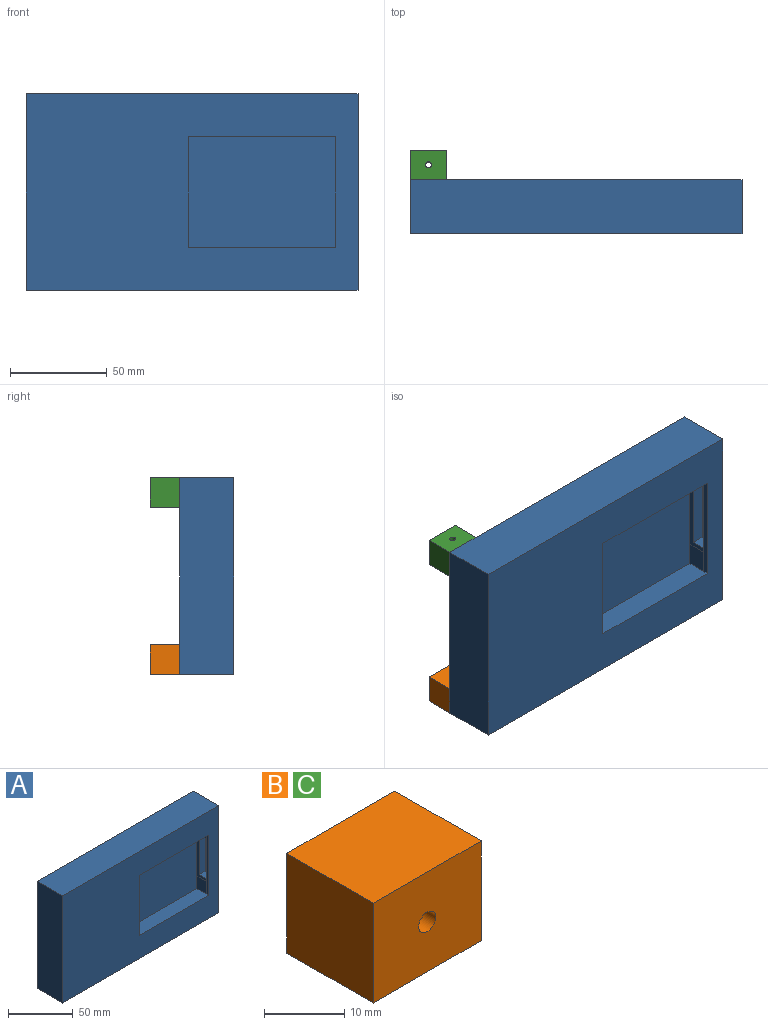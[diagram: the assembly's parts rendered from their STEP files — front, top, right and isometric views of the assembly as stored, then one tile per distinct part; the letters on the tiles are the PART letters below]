
ASSEMBLY  parts=3 mates=2
PART A: 29 faces, bbox 171.5x27.9x101.6 mm
  f0: plane 101.6x27.94mm, normal (-1,0,0), area 2838.7mm2, adj f1,f2,f3,f8
  f1: plane 171.45x27.94mm, normal (0,0,-1), area 4790.3mm2, adj f0,f3,f8,f14
  f2: plane 171.45x27.94mm, normal (0,0,1), area 4790.3mm2, adj f0,f3,f8,f14
  f3: plane 171.45x101.6mm, normal (0,1,0), area 17419.3mm2, adj f0,f1,f2,f14
  f4: plane 57.15x2.54mm, normal (-1,0,0), area 145.2mm2, adj f5,f7,f8,f13
  f5: plane 76.2x12.7mm, normal (0,0,1), area 967.7mm2, adj f4,f6,f8,f9,f19
  f6: plane 57.15x12.7mm, normal (1,0,0), area 725.8mm2, adj f5,f7,f8,f9
  f7: plane 76.2x12.7mm, normal (0,0,-1), area 967.7mm2, adj f4,f6,f8,f9,f19
  f8: plane 171.45x101.6mm, normal (0,-1,0), area 13064.5mm2, adj f0,f1,f2,f4,f5,f6,f7,f14
  f9: plane 76.2x57.15mm, normal (0,-1,0), area 4354.8mm2, adj f5,f6,f7,f19
  f10: plane 12.7x6.35mm, normal (0,0,-1), area 80.6mm2, adj f11,f13,f14,f28
  f11: plane 38.1x6.35mm, normal (0,-1,0), area 241.9mm2, adj f10,f12,f14,f28
  f12: plane 12.7x6.35mm, normal (0,0,1), area 80.6mm2, adj f11,f13,f14,f28
  f13: plane 168.91x96.52mm, normal (0,1,0), area 11235.5mm2, adj f4,f10,f12,f14,f15,f16,f17,f19
  f14: plane 101.6x27.94mm, normal (1,0,0), area 2354.8mm2, adj f1,f2,f3,f8,f10,f11,f12,f13
  f15: plane 96.52x22.86mm, normal (1,0,0), area 2206.4mm2, adj f13,f16,f17,f18
  f16: plane 166.37x22.86mm, normal (0,0,1), area 3803.2mm2, adj f13,f15,f18,f27
  f17: plane 166.37x22.86mm, normal (0,0,-1), area 3803.2mm2, adj f13,f15,f18,f27
  f18: plane 166.37x96.52mm, normal (0,-1,0), area 16058mm2, adj f15,f16,f17,f27
  f19: plane 62.23x12.7mm, normal (1,0,0), area 209.7mm2, adj f5,f7,f9,f13,f20,f22,f23
  f20: plane 78.74x12.7mm, normal (0,0,-1), area 1000mm2, adj f13,f19,f21,f23
  f21: plane 62.23x12.7mm, normal (-1,0,0), area 790.3mm2, adj f13,f20,f22,f23
  f22: plane 78.74x12.7mm, normal (0,0,1), area 1000mm2, adj f13,f19,f21,f23
  f23: plane 78.74x62.23mm, normal (0,1,0), area 4900mm2, adj f19,f20,f21,f22
  f24: plane 15.24x3.81mm, normal (0,0,1), area 58.1mm2, adj f13,f25,f27,f28
  f25: plane 43.18x3.81mm, normal (0,1,0), area 164.5mm2, adj f24,f26,f27,f28
  f26: plane 15.24x3.81mm, normal (0,0,-1), area 58.1mm2, adj f13,f25,f27,f28
  f27: plane 96.52x22.86mm, normal (-1,0,0), area 1548.4mm2, adj f13,f16,f17,f18,f24,f25,f26
  f28: plane 43.18x15.24mm, normal (-1,0,0), area 174.2mm2, adj f10,f11,f12,f13,f24,f25,f26
PART B: 7 faces, bbox 19.1x15.2x15.2 mm
  f0: plane 15.24x15.24mm, normal (-1,0,0), area 232.3mm2, adj f1,f4,f5,f6
  f1: plane 19.05x15.24mm, normal (0,0,-1), area 290.3mm2, adj f0,f2,f5,f6
  f2: plane 15.24x15.24mm, normal (1,0,0), area 232.3mm2, adj f1,f4,f5,f6
  f3: cylinder r=1.5mm len=15.24mm, axis (0,1,0), area 143.6mm2, adj f5,f6
  f4: plane 19.05x15.24mm, normal (0,0,1), area 290.3mm2, adj f0,f2,f5,f6
  f5: plane 19.05x15.24mm, normal (0,-1,0), area 283.3mm2, adj f0,f1,f2,f3,f4
  f6: plane 19.05x15.24mm, normal (0,1,0), area 283.3mm2, adj f0,f1,f2,f3,f4
PART C: same geometry as B
PLACE A t=(-45.54,-20.77,63.81)mm fixed
PLACE B rot(axis=(-1,0,0),90deg) t=(-109.25,-11.53,9.53)mm
PLACE C rot(axis=(1,0,0),90deg) t=(-109.25,-14.76,111.13)mm
MATE fastened C.f6 <-> A.f2  axis (0,0,1) through (-116.03,-20.77,111.13)mm
MATE fastened B.f6 <-> A.f1  axis (0,0,-1) through (-116.03,-20.77,9.53)mm
